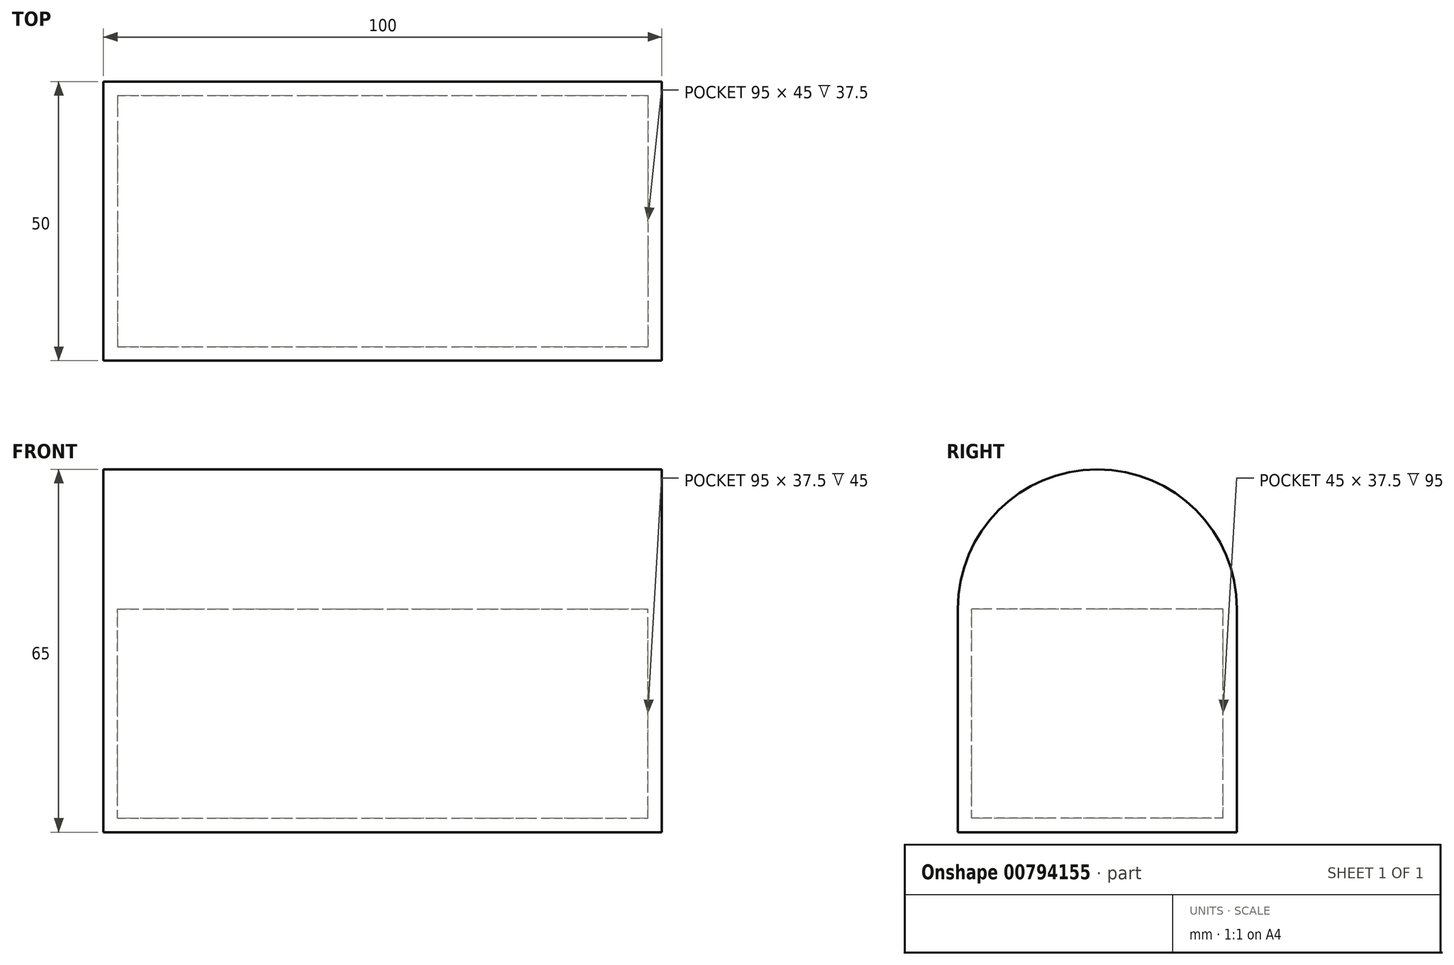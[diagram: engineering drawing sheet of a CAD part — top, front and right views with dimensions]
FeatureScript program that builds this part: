
annotation { "Feature Type Name" : "Feature", "Feature Type Description" : "" }
export const myFeature = defineFeature(function(context is Context, id is Id, definition is map)
    precondition{}
    {
        {
            var Q0;
            Q0=qCreatedBy(makeId("Top.planeOp"),FACE);
            var sketch = newSketch(context, id + "F0", { "sketchPlane" : qUnion([Q0])});
            skLineSegment(sketch, "E0.bottom", {"start": v(-50, 25) * mm, "end": v(50, 25) * mm});
            skLineSegment(sketch, "E0.top", {"start": v(-50, -25) * mm, "end": v(50, -25) * mm});
            skLineSegment(sketch, "E0.left", {"start": v(-50, 25) * mm, "end": v(-50, -25) * mm});
            skLineSegment(sketch, "E0.right", {"start": v(50, 25) * mm, "end": v(50, -25) * mm});
            skSolve(sketch);
        }
        {
            var Q0;
            Q0=makeQuery(id+"F0.imprint","IMPRINT",FACE,{"disambiguationData":[TD([[makeQuery(id+"F0.imprint","IMPRINT",EDGE,{"derivedFrom":sQuery(id+"F0.wireOp",EDGE,"E0.bottom")}),-1.0]])]});
            extrude(context, id + "F1", {"entities" : qUnion([Q0]), "oppositeDirection" : true, "depth" : 40 * mm, "offsetDistance" : 25 * mm});
        }
        {
            var Q0;
            Q0=makeQuery(id+"F1.opExtrude","CAP_FACE",FACE,{"disambiguationData":[OSD([sQuery(id+"F0.wireOp",EDGE,"E0.bottom"),sQuery(id+"F0.wireOp",EDGE,"E0.top"),sQuery(id+"F0.wireOp",EDGE,"E0.left"),sQuery(id+"F0.wireOp",EDGE,"E0.right")])],"isStart":true});
            shell(context, id + "F2", {"entities" : qUnion([Q0]), "thickness" : 2.5 * mm});
        }
        {
            var Q0;
            Q0=qCreatedBy(makeId("Right.planeOp"),FACE);
            var sketch = newSketch(context, id + "F3", { "sketchPlane" : qUnion([Q0])});
            skArc(sketch, "E1", {"start": v(25, 0) * mm, "mid": v(0, 25) * mm, "end": v(-25, 0) * mm});
            skLineSegment(sketch, "E2", {"start": v(25, 0) * mm, "end": v(-25, 0) * mm});
            skSolve(sketch);
        }
        {
            var Q0;
            Q0=makeQuery(id+"F3.imprint","IMPRINT",FACE,{"disambiguationData":[TD([[makeQuery(id+"F3.imprint","IMPRINT",EDGE,{"derivedFrom":sQuery(id+"F3.wireOp",EDGE,"E1")}),1.0]])]});
            extrude(context, id + "F4", {"entities" : qUnion([Q0]), "operationType" : NewBodyOperationType.ADD, "endBound" : BoundingType.SYMMETRIC, "depth" : 100 * mm, "offsetDistance" : 25 * mm});
        }
    });
